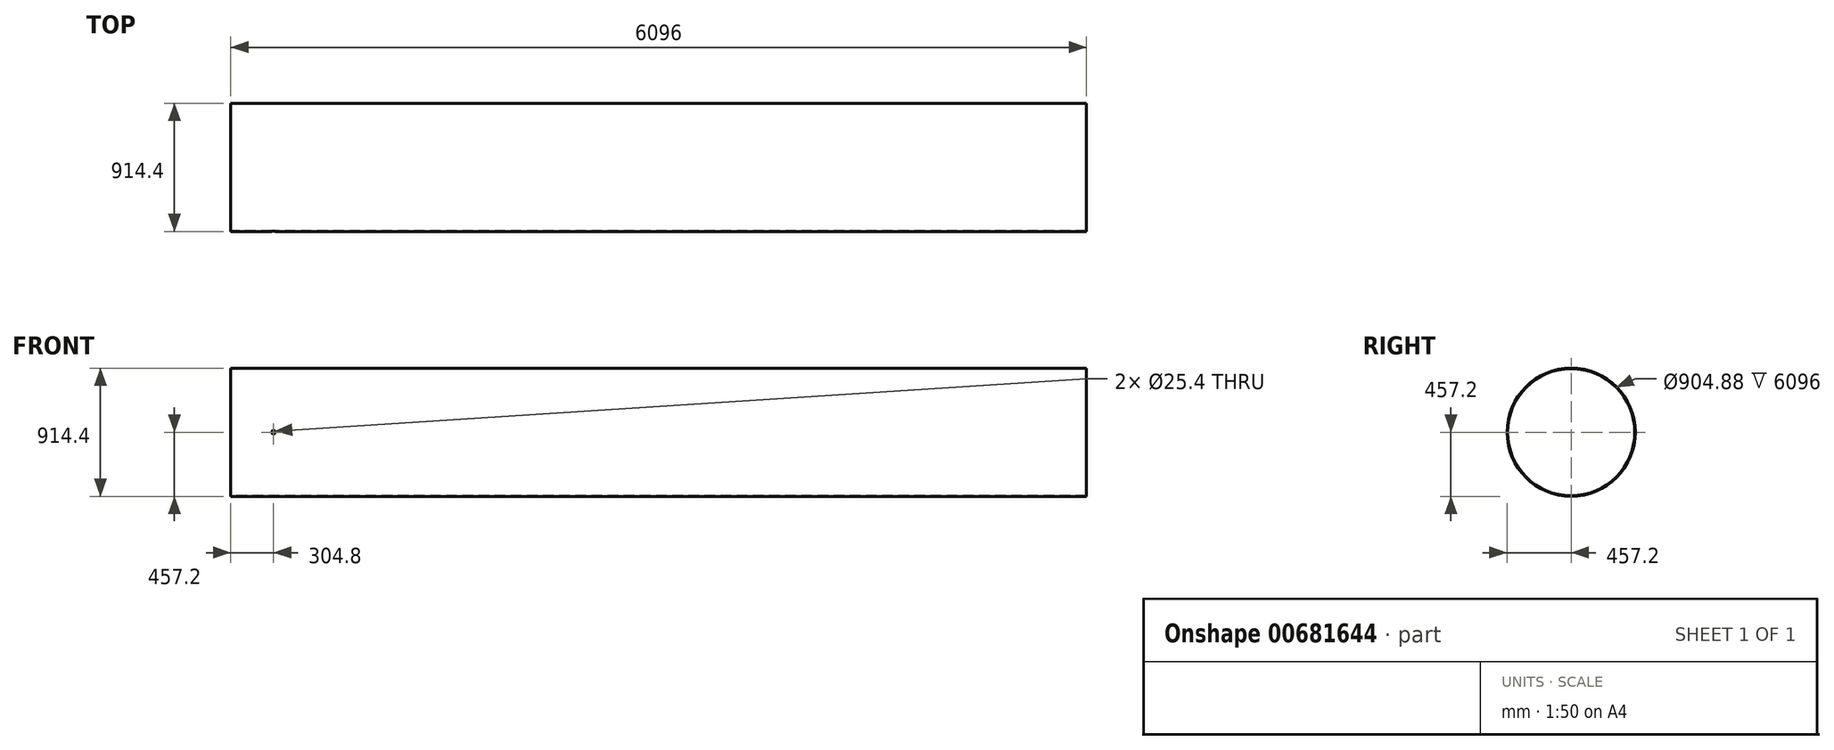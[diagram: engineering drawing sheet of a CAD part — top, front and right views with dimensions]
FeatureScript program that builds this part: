
annotation { "Feature Type Name" : "Feature", "Feature Type Description" : "" }
export const myFeature = defineFeature(function(context is Context, id is Id, definition is map)
    precondition{}
    {
        {
            var Q0;
            Q0=qCreatedBy(makeId("Right.planeOp"),FACE);
            var sketch = newSketch(context, id + "F0", { "sketchPlane" : qUnion([Q0])});
            skCircle(sketch, "E0", {"center": v(0, 0) * mm, "radius": 457.2 * mm});
            skCircle(sketch, "E1", {"center": v(0, 0) * mm, "radius": 452.44 * mm});
            skSolve(sketch);
        }
        {
            var Q0;
            Q0=makeQuery(id+"F0.imprint","IMPRINT",FACE,{"disambiguationData":[TD([[makeQuery(id+"F0.imprint","IMPRINT",EDGE,{"derivedFrom":sQuery(id+"F0.wireOp",EDGE,"E0")}),1.0]])]});
            extrude(context, id + "F1", {"entities" : qUnion([Q0]), "depth" : 6096 * mm, "offsetDistance" : 25.4 * mm});
        }
        {
            var Q0;
            Q0=qCreatedBy(makeId("Front.planeOp"),FACE);
            var sketch = newSketch(context, id + "F2", { "sketchPlane" : qUnion([Q0])});
            skLineSegment(sketch, "E2", {"start": v(0, 0) * mm, "end": v(304.8, 0) * mm});
            skCircle(sketch, "E3", {"center": v(304.8, 0) * mm, "radius": 12.7 * mm});
            skSolve(sketch);
        }
        {
            var Q0;
            Q0=makeQuery(id+"F2.imprint","IMPRINT",FACE,{"disambiguationData":[TD([[makeQuery(id+"F2.imprint","IMPRINT",EDGE,{"derivedFrom":sQuery(id+"F2.wireOp",EDGE,"E3")}),1.0]])]});
            extrude(context, id + "F3", {"entities" : qUnion([Q0]), "operationType" : NewBodyOperationType.REMOVE, "endBound" : BoundingType.SYMMETRIC, "depth" : 1016 * mm, "offsetDistance" : 25.4 * mm});
        }
    });
